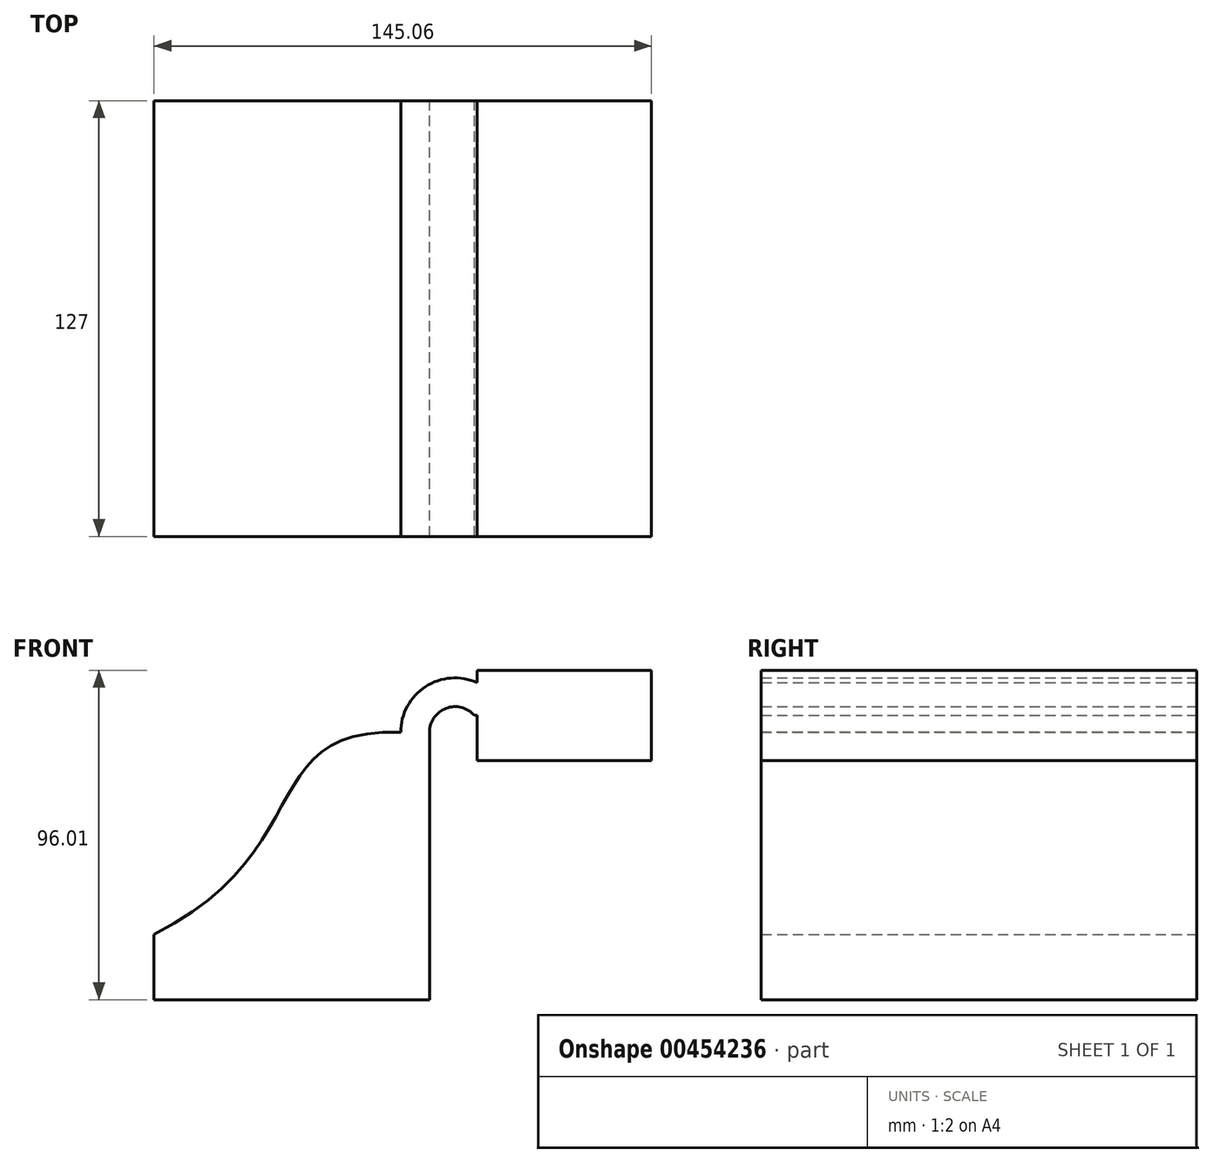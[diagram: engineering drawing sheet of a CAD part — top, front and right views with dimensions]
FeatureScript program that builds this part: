
annotation { "Feature Type Name" : "Feature", "Feature Type Description" : "" }
export const myFeature = defineFeature(function(context is Context, id is Id, definition is map)
    precondition{}
    {
        {
            var Q0;
            Q0=qCreatedBy(makeId("Front.planeOp"),FACE);
            var sketch = newSketch(context, id + "F0", { "sketchPlane" : qUnion([Q0])});
            skLineSegment(sketch, "E0.bottom", {"start": v(40.16, -9.52) * mm, "end": v(-40.16, -9.53) * mm});
            skLineSegment(sketch, "E0.top", {"start": v(40.16, 9.53) * mm, "end": v(-40.16, 9.53) * mm});
            skLineSegment(sketch, "E0.left", {"start": v(40.16, -9.52) * mm, "end": v(40.16, 9.53) * mm});
            skLineSegment(sketch, "E0.right", {"start": v(-40.16, -9.53) * mm, "end": v(-40.16, 9.53) * mm});
            skPoint(sketch, "E0.middle", {"position": v(0, 0) * mm});
            skLineSegment(sketch, "E1.bottom", {"start": v(104.9, 60.13) * mm, "end": v(54.1, 60.13) * mm});
            skLineSegment(sketch, "E1.top", {"start": v(104.9, 86.48) * mm, "end": v(54.1, 86.48) * mm});
            skLineSegment(sketch, "E1.left", {"start": v(104.9, 60.13) * mm, "end": v(104.9, 86.48) * mm});
            skLineSegment(sketch, "E1.right", {"start": v(54.1, 60.13) * mm, "end": v(54.1, 86.48) * mm});
            skPoint(sketch, "E1.middle", {"position": v(79.5, 73.3) * mm});
            skLineSegment(sketch, "E2", {"start": v(40.16, 9.53) * mm, "end": v(40.16, 68.4) * mm});
            skArc(sketch, "E3", {"start": v(40.16, 68.4) * mm, "mid": v(45, 75.39) * mm, "end": v(53.24, 73.3) * mm});
            skLineSegment(sketch, "E4", {"start": v(53.24, 73.3) * mm, "end": v(79.5, 73.3) * mm});
            skLineSegment(sketch, "E5.0", {"start": v(56.25, 81.69) * mm, "end": v(79.5, 81.69) * mm});
            skArc(sketch, "E5.1", {"start": v(31.78, 68.4) * mm, "mid": v(40.06, 82.33) * mm, "end": v(56.25, 81.69) * mm});
            skLineSegment(sketch, "E5.2", {"start": v(31.78, 9.53) * mm, "end": v(31.78, 68.4) * mm});
            skLineSegment(sketch, "E6", {"start": v(79.5, 86.48) * mm, "end": v(79.5, 60.13) * mm});
            skFitSpline(sketch, "E7", {"points": [v(-40.16, 9.53) * mm, v(31.78, 68.4) * mm], "startDerivative": vector(145.6, 72.63) * mm, "endDerivative": vector(128.4, -3.63) * mm});
            skSolve(sketch);
        }
        {
            var Q0;
            Q0 = qSketchRegion(id + "F0", true);
            extrude(context, id + "F1", {"entities" : qUnion([Q0]), "endBound" : BoundingType.SYMMETRIC, "depth" : 127 * mm});
        }
    });
